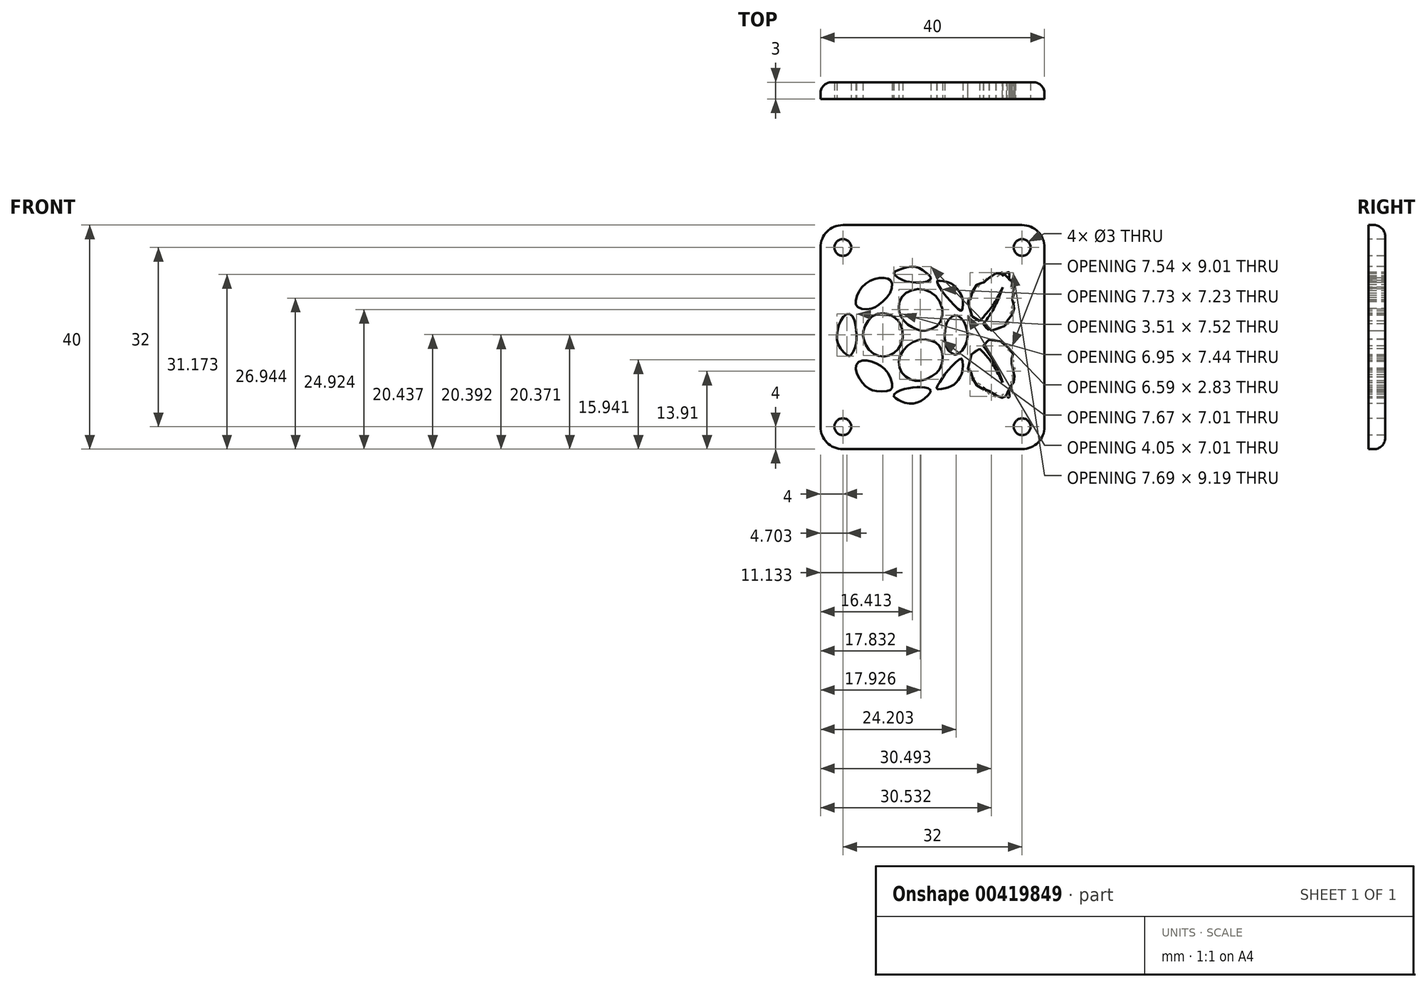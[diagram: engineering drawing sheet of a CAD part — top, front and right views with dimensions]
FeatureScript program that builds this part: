
annotation { "Feature Type Name" : "Feature", "Feature Type Description" : "" }
export const myFeature = defineFeature(function(context is Context, id is Id, definition is map)
    precondition{}
    {
        {
            var Q0;
            Q0=qCreatedBy(makeId("Front.planeOp"),FACE);
            var sketch = newSketch(context, id + "F0", { "sketchPlane" : qUnion([Q0])});
            skFitSpline(sketch, "E0", {"points": [v(-6.88, 6.47) * mm, v(-8.05, 7.87) * mm, v(-8.9, 9.2) * mm, v(-9.16, 9.72) * mm, v(-9.16, 10.05) * mm, v(-8.8, 10.08) * mm, v(-7.14, 9.79) * mm, v(-5.97, 9.04) * mm, v(-4.93, 7.68) * mm, v(-4.54, 6.05) * mm, v(-4.7, 4.91) * mm, v(-4.8, 4.72) * mm, v(-5.03, 4.72) * mm, v(-6.88, 6.47) * mm]});
            skFitSpline(sketch, "E1", {"points": [v(-7.82, 0.4) * mm, v(-7.63, 1.92) * mm, v(-7.27, 2.87) * mm, v(-6.4, 3.78) * mm, v(-5.78, 3.9) * mm, v(-4.87, 3.39) * mm, v(-4.05, 1.99) * mm, v(-3.76, 0) * mm, v(-4.35, -1.88) * mm, v(-5.61, -3.08) * mm, v(-6.33, -3.02) * mm, v(-7.34, -2.1) * mm, v(-7.73, -0.71) * mm, v(-7.82, 0.4) * mm]});
            skFitSpline(sketch, "E2", {"points": [v(-6.53, -5.2) * mm, v(-5.11, -3.92) * mm, v(-4.78, -3.84) * mm, v(-4.58, -4.7) * mm, v(-4.65, -6.08) * mm, v(-5.07, -7.17) * mm, v(-5.58, -7.91) * mm, v(-6.1, -8.42) * mm, v(-6.75, -8.81) * mm, v(-7.52, -9.1) * mm, v(-8.34, -9.25) * mm, v(-9.2, -9.3) * mm, v(-9.24, -9) * mm, v(-8.79, -8.19) * mm, v(-7.94, -6.85) * mm, v(-6.53, -5.2) * mm]});
            skFitSpline(sketch, "E3", {"points": [v(-15.9, -5.41) * mm, v(-15.5, -2.78) * mm, v(-12.91, -0.64) * mm, v(-10.22, -0.62) * mm, v(-8.56, -1.91) * mm, v(-8.37, -4.9) * mm, v(-9.7, -6.73) * mm, v(-12.3, -7.79) * mm, v(-14.4, -7.33) * mm, v(-15.9, -5.41) * mm]});
            skFitSpline(sketch, "E4", {"points": [v(-15.08, 2.88) * mm, v(-16.02, 5.14) * mm, v(-15.29, 7.38) * mm, v(-12.14, 8.56) * mm, v(-8.87, 6.69) * mm, v(-8.6, 2.7) * mm, v(-11.36, 1.14) * mm, v(-13.24, 1.55) * mm, v(-15.08, 2.88) * mm]});
            skFitSpline(sketch, "E5", {"points": [v(-13.53, 9.8) * mm, v(-15.08, 10.1) * mm, v(-16.9, 11.33) * mm, v(-16.18, 11.93) * mm, v(-13.37, 12.58) * mm, v(-11.27, 11.62) * mm, v(-10.3, 10.44) * mm, v(-11.71, 9.76) * mm, v(-13.53, 9.8) * mm]});
            skFitSpline(sketch, "E6", {"points": [v(-19.56, 5.82) * mm, v(-21.18, 5.03) * mm, v(-23.37, 5.37) * mm, v(-23.68, 6.51) * mm, v(-22.67, 8.83) * mm, v(-20.5, 10.32) * mm, v(-18.36, 10.53) * mm, v(-17.34, 9.92) * mm, v(-17.53, 7.9) * mm, v(-19.56, 5.82) * mm]});
            skFitSpline(sketch, "E7", {"points": [v(-22.34, 1.06) * mm, v(-21.22, 3.25) * mm, v(-19.12, 4.3) * mm, v(-16.87, 3.58) * mm, v(-15.54, 1.91) * mm, v(-15.56, -1.2) * mm, v(-17.26, -3.03) * mm, v(-19.2, -3.44) * mm, v(-21.24, -2.36) * mm, v(-22.29, -0.33) * mm, v(-22.34, 1.06) * mm]});
            skFitSpline(sketch, "E8", {"points": [v(-23.62, -4.97) * mm, v(-22.34, -4.16) * mm, v(-20.12, -4.64) * mm, v(-17.97, -6.38) * mm, v(-17.2, -8.95) * mm, v(-17.78, -9.53) * mm, v(-20.14, -9.63) * mm, v(-21.67, -8.99) * mm, v(-23.25, -7.06) * mm, v(-23.62, -4.97) * mm]});
            skFitSpline(sketch, "E9", {"points": [v(-23.54, 0.4) * mm, v(-23.74, -1.58) * mm, v(-24.59, -3.27) * mm, v(-24.95, -3.38) * mm, v(-26.54, -1.84) * mm, v(-27.04, 0.43) * mm, v(-26.27, 3.11) * mm, v(-25.01, 4.16) * mm, v(-24, 3.17) * mm, v(-23.54, 0.4) * mm]});
            skFitSpline(sketch, "E10", {"points": [v(-14.25, -9.1) * mm, v(-12.3, -8.93) * mm, v(-10.8, -9.12) * mm, v(-10.3, -9.6) * mm, v(-11.53, -11.05) * mm, v(-13.3, -11.81) * mm, v(-15.22, -11.62) * mm, v(-16.39, -11.04) * mm, v(-16.93, -10.47) * mm, v(-16.22, -9.7) * mm, v(-14.25, -9.1) * mm]});
            skFitSpline(sketch, "E11", {"points": [v(-1.56, 2.88) * mm, v(-2.43, 3.23) * mm, v(-3.4, 4.76) * mm, v(-3.6, 7.11) * mm, v(-3.25, 6.73) * mm, v(-2.95, 8.34) * mm, v(-2.63, 7.9) * mm, v(-2.05, 9.44) * mm, v(-1.83, 8.9) * mm, v(-0.96, 10.4) * mm, v(-0.8, 9.8) * mm, v(0, 10.91) * mm, v(0.27, 10.42) * mm, v(1.26, 11.38) * mm, v(1.4, 10.72) * mm, v(2.43, 11.54) * mm, v(2.49, 11) * mm, v(3.6, 11.6) * mm, v(3.73, 10.07) * mm, v(4.15, 10.4) * mm, v(4, 8.7) * mm, v(4.49, 8.93) * mm, v(4.21, 7.52) * mm, v(4.78, 7.9) * mm, v(4.23, 6.38) * mm, v(4.78, 6.5) * mm, v(4.07, 5.26) * mm, v(4.62, 5.16) * mm, v(3.82, 4.22) * mm, v(4.38, 3.99) * mm, v(3.27, 2.92) * mm, v(3.7, 2.74) * mm, v(2.15, 1.55) * mm, v(0.12, 1.27) * mm, v(-0.92, 2.35) * mm], "startDerivative": vector(-32.85, 9.46) * mm, "endDerivative": vector(-26.34, 38.43) * mm});
            skFitSpline(sketch, "E12", {"points": [v(-0.92, 2.35) * mm, v(0.59, 4.5) * mm, v(1.7, 6.67) * mm, v(2.52, 8.9) * mm], "startDerivative": vector(4.62, 6.23) * mm, "endDerivative": vector(2.4, 6.86) * mm});
            skFitSpline(sketch, "E13", {"points": [v(-1.56, 2.88) * mm, v(-0.37, 4.2) * mm, v(1.06, 6.12) * mm, v(2.52, 8.9) * mm], "startDerivative": vector(4.08, 4.42) * mm, "endDerivative": vector(3.7, 7.63) * mm});
            skFitSpline(sketch, "E14", {"points": [v(-1.56, -2.1) * mm, v(-2.64, -2.6) * mm, v(-3.5, -4.37) * mm, v(-3.65, -6.28) * mm, v(-3.28, -5.94) * mm, v(-2.94, -7.79) * mm, v(-2.64, -7.15) * mm, v(-2.07, -8.6) * mm, v(-1.83, -8.14) * mm, v(-0.92, -9.57) * mm, v(-0.92, -9.02) * mm, v(0.12, -10.19) * mm, v(0.12, -9.64) * mm, v(1.29, -10.67) * mm, v(1.34, -9.87) * mm, v(2.52, -10.88) * mm, v(2.52, -10.19) * mm, v(3.66, -10.79) * mm, v(3.66, -9.32) * mm, v(4.12, -9.64) * mm, v(4.07, -7.79) * mm, v(4.53, -8.17) * mm, v(4.2, -6.74) * mm, v(4.74, -7.09) * mm, v(4.23, -5.6) * mm, v(4.83, -5.7) * mm, v(4.1, -4.46) * mm, v(4.61, -4.35) * mm, v(3.8, -3.4) * mm, v(4.48, -3.18) * mm, v(3.28, -2.12) * mm, v(3.77, -2) * mm, v(2.15, -0.8) * mm, v(0.42, -0.4) * mm, v(-0.62, -0.95) * mm, v(-0.92, -1.59) * mm], "startDerivative": vector(-39.2, -12.29) * mm, "endDerivative": vector(-8.47, -28.8) * mm});
            skFitSpline(sketch, "E15", {"points": [v(-0.92, -1.59) * mm, v(0.37, -3.44) * mm, v(1.64, -5.72) * mm, v(2.52, -8.12) * mm], "startDerivative": vector(4.08, -5.63) * mm, "endDerivative": vector(2.33, -7.15) * mm});
            skFitSpline(sketch, "E16", {"points": [v(-1.56, -2.1) * mm, v(-0.2, -3.57) * mm, v(1.15, -5.55) * mm, v(2.52, -8.12) * mm], "startDerivative": vector(4.58, -4.64) * mm, "endDerivative": vector(3.7, -7.24) * mm});
            skCircle(sketch, "E17", {"center": v(-26, 16) * mm, "radius": 1.5 * mm});
            skCircle(sketch, "E18", {"center": v(-26, -16) * mm, "radius": 1.5 * mm});
            skCircle(sketch, "E19", {"center": v(6, -16) * mm, "radius": 1.5 * mm});
            skCircle(sketch, "E20", {"center": v(6, 16) * mm, "radius": 1.5 * mm});
            skLineSegment(sketch, "E21.bottom", {"start": v(-26, 20) * mm, "end": v(6, 20) * mm});
            skLineSegment(sketch, "E21.top", {"start": v(-26, -20) * mm, "end": v(6, -20) * mm});
            skLineSegment(sketch, "E21.left", {"start": v(-30, 16) * mm, "end": v(-30, -16) * mm});
            skLineSegment(sketch, "E21.right", {"start": v(10, 16) * mm, "end": v(10, -16) * mm});
            skPoint(sketch, "E22.visualSharp", {"position": v(10, 20) * mm});
            skArc(sketch, "E22.filletArc", {"start": v(10, 16) * mm, "mid": v(8.83, 18.83) * mm, "end": v(6, 20) * mm});
            skPoint(sketch, "E23.visualSharp", {"position": v(-30, 20) * mm});
            skArc(sketch, "E23.filletArc", {"start": v(-26, 20) * mm, "mid": v(-28.83, 18.83) * mm, "end": v(-30, 16) * mm});
            skPoint(sketch, "E24.visualSharp", {"position": v(-30, -20) * mm});
            skArc(sketch, "E24.filletArc", {"start": v(-30, -16) * mm, "mid": v(-28.83, -18.83) * mm, "end": v(-26, -20) * mm});
            skPoint(sketch, "E25.visualSharp", {"position": v(10, -20) * mm});
            skArc(sketch, "E25.filletArc", {"start": v(6, -20) * mm, "mid": v(8.83, -18.83) * mm, "end": v(10, -16) * mm});
            skSolve(sketch);
        }
        {
            var Q0;
            Q0 = qSketchRegion(id + "F0", true);
            extrude(context, id + "F1", {"entities" : qUnion([Q0]), "oppositeDirection" : true, "depth" : 3 * mm});
        }
        {
            var Q0;
            Q0=makeQuery(id+"F1.opExtrude","CAP_EDGE",EDGE,{"disambiguationData":[OSD([sQuery(id+"F0.wireOp",EDGE,"E21.top")])],"isStart":false});
            fillet(context, id + "F2", {"entities" : qUnion([Q0]), "radius" : 2 * mm, "tangentPropagation" : true, "allowEdgeOverflow" : false});
        }
    });
